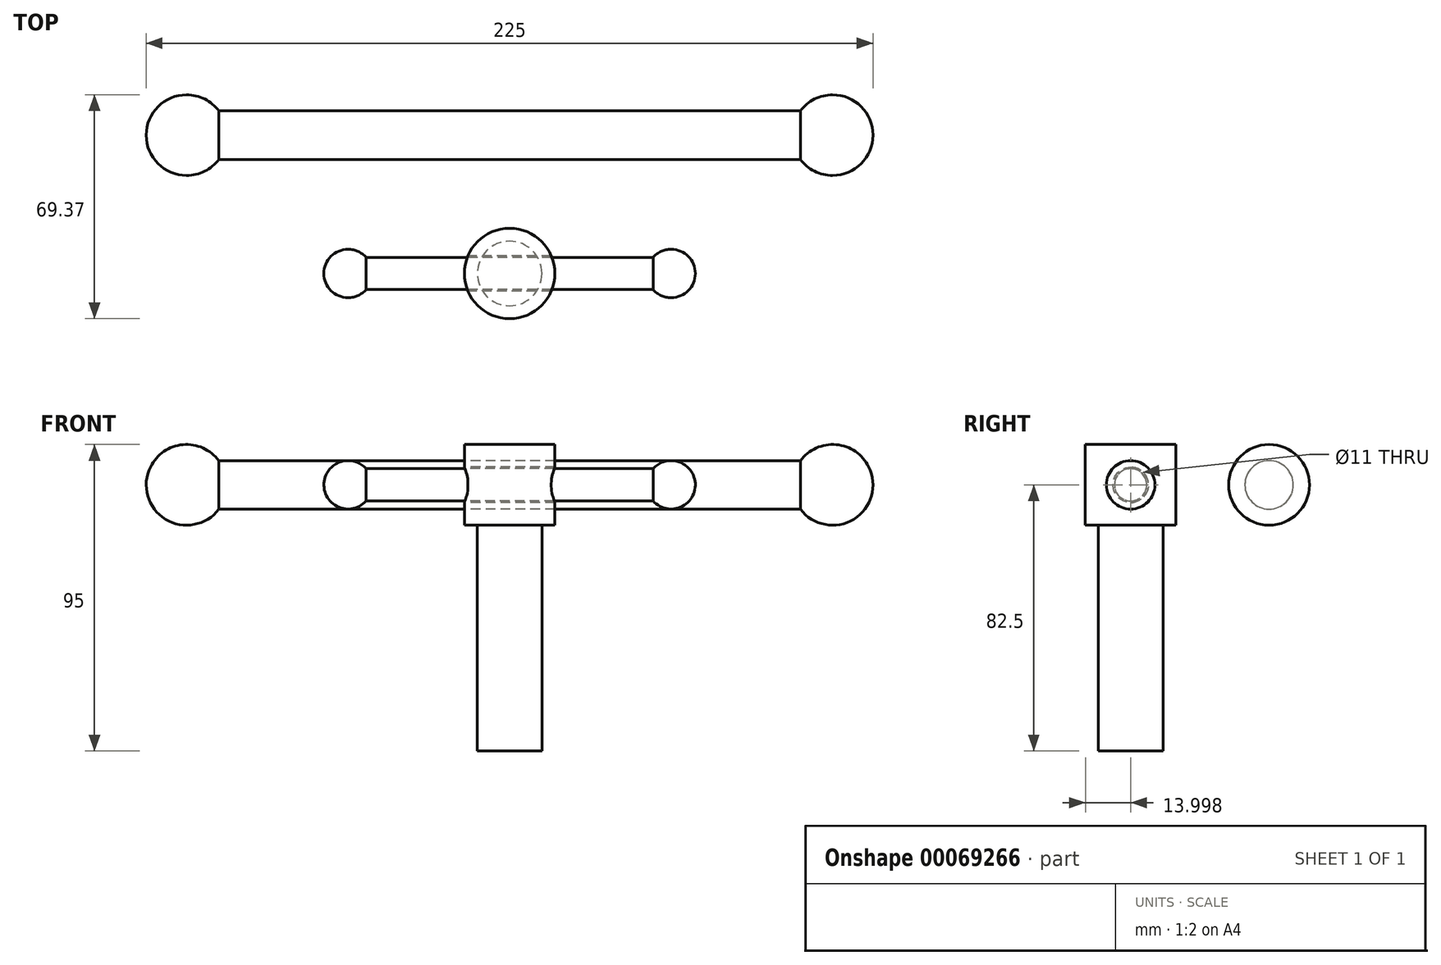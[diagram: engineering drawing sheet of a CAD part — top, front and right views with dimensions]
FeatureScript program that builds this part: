
annotation { "Feature Type Name" : "Feature", "Feature Type Description" : "" }
export const myFeature = defineFeature(function(context is Context, id is Id, definition is map)
    precondition{}
    {
        {
            var Q0;
            Q0=qCreatedBy(makeId("Right.planeOp"),FACE);
            var sketch = newSketch(context, id + "F0", { "sketchPlane" : qUnion([Q0])});
            skCircle(sketch, "E0", {"center": v(0, 0) * mm, "radius": 7.5 * mm});
            skSolve(sketch);
        }
        {
            var Q0;
            Q0=makeQuery(id+"F0.imprint","IMPRINT",FACE,{"disambiguationData":[TD([[makeQuery(id+"F0.imprint","IMPRINT",EDGE,{"derivedFrom":sQuery(id+"F0.wireOp",EDGE,"E0")}),1.0]])]});
            extrude(context, id + "F1", {"entities" : qUnion([Q0]), "endBound" : BoundingType.SYMMETRIC, "depth" : 200 * mm});
        }
        {
            var Q0;
            Q0=makeQuery(id+"F1.opExtrude","CAP_FACE",FACE,{"disambiguationData":[OSD([sQuery(id+"F0.wireOp",EDGE,"E0")])],"isStart":true});
            var sketch = newSketch(context, id + "F2", { "sketchPlane" : qUnion([Q0])});
            skArc(sketch, "E1", {"start": v(12.5, 0) * mm, "mid": v(0, 12.5) * mm, "end": v(-12.5, 0) * mm});
            skLineSegment(sketch, "E2", {"start": v(-12.5, 0) * mm, "end": v(12.5, 0) * mm});
            skSolve(sketch);
        }
        {
            var Q0;
            Q0 = qSketchRegion(id + "F2", true);
            var Q1;
            Q1=sQuery(id+"F2.wireOp",EDGE,"E2");
            revolve(context, id + "F3", {"operationType" : NewBodyOperationType.ADD, "entities" : qUnion([Q0]), "axis" : qUnion([Q1]), "revolveType" : RevolveType.FULL});
        }
        {
            var Q0;
            Q0=makeQuery(id+"F1.opExtrude","CAP_FACE",FACE,{"disambiguationData":[OSD([sQuery(id+"F0.wireOp",EDGE,"E0")])],"isStart":false});
            var sketch = newSketch(context, id + "F4", { "sketchPlane" : qUnion([Q0])});
            skArc(sketch, "E3.0", {"start": v(-12.5, 0) * mm, "mid": v(0, 12.5) * mm, "end": v(12.5, 0) * mm});
            skLineSegment(sketch, "E4.0", {"start": v(12.5, 0) * mm, "end": v(-12.5, 0) * mm});
            skSolve(sketch);
        }
        {
            var Q0;
            Q0 = qSketchRegion(id + "F4", true);
            var Q1;
            Q1=sQuery(id+"F4.wireOp",EDGE,"E4.0");
            revolve(context, id + "F5", {"operationType" : NewBodyOperationType.ADD, "entities" : qUnion([Q0]), "axis" : qUnion([Q1]), "revolveType" : RevolveType.FULL});
        }
        {
            var Q0;
            Q0=qCreatedBy(makeId("Top.planeOp"),FACE);
            var sketch = newSketch(context, id + "F6", { "sketchPlane" : qUnion([Q0])});
            skCircle(sketch, "E5", {"center": v(0, -42.87) * mm, "radius": 14 * mm});
            skSolve(sketch);
        }
        {
            var Q0;
            Q0 = qSketchRegion(id + "F6", true);
            extrude(context, id + "F7", {"entities" : qUnion([Q0]), "endBound" : BoundingType.SYMMETRIC, "depth" : 25 * mm});
        }
        {
            var Q0;
            Q0=qCreatedBy(makeId("Right.planeOp"),FACE);
            var sketch = newSketch(context, id + "F8", { "sketchPlane" : qUnion([Q0])});
            skCircle(sketch, "E6", {"center": v(-42.87, 0) * mm, "radius": 5.5 * mm});
            skLineSegment(sketch, "E7", {"start": v(-42.87, 0) * mm, "end": v(-42.87, 12.5) * mm, "construction": true});
            skSolve(sketch);
        }
        {
            var Q0;
            Q0 = qSketchRegion(id + "F8", true);
            extrude(context, id + "F9", {"entities" : qUnion([Q0]), "operationType" : NewBodyOperationType.REMOVE, "endBound" : BoundingType.THROUGH_ALL, "depth" : 25 * mm, "hasSecondDirection" : true, "secondDirectionBound" : SecondDirectionBoundingType.THROUGH_ALL, "secondDirectionOppositeDirection" : true, "secondDirectionDepth" : 25 * mm});
        }
        {
            var Q0;
            Q0=qCreatedBy(makeId("Right.planeOp"),FACE);
            var sketch = newSketch(context, id + "F10", { "sketchPlane" : qUnion([Q0])});
            skCircle(sketch, "E8", {"center": v(-42.87, 0) * mm, "radius": 5 * mm});
            skSolve(sketch);
        }
        {
            var Q0;
            Q0 = qSketchRegion(id + "F10", true);
            extrude(context, id + "F11", {"entities" : qUnion([Q0]), "endBound" : BoundingType.SYMMETRIC, "depth" : 100 * mm});
        }
        {
            var Q0;
            Q0=makeQuery(id+"F11.opExtrude","CAP_FACE",FACE,{"disambiguationData":[OSD([sQuery(id+"F10.wireOp",EDGE,"E8")])],"isStart":false});
            var sketch = newSketch(context, id + "F12", { "sketchPlane" : qUnion([Q0])});
            skArc(sketch, "E9", {"start": v(-35.37, 0) * mm, "mid": v(-42.87, 7.5) * mm, "end": v(-50.37, 0) * mm});
            skLineSegment(sketch, "E10", {"start": v(-50.37, 0) * mm, "end": v(-35.37, 0) * mm});
            skSolve(sketch);
        }
        {
            var Q0;
            Q0 = qSketchRegion(id + "F12", true);
            var Q1;
            Q1=sQuery(id+"F12.wireOp",EDGE,"E10");
            revolve(context, id + "F13", {"operationType" : NewBodyOperationType.ADD, "entities" : qUnion([Q0]), "axis" : qUnion([Q1]), "revolveType" : RevolveType.FULL});
        }
        {
            var Q0;
            Q0=makeQuery(id+"F11.opExtrude","CAP_FACE",FACE,{"disambiguationData":[OSD([sQuery(id+"F10.wireOp",EDGE,"E8")])],"isStart":true});
            var sketch = newSketch(context, id + "F14", { "sketchPlane" : qUnion([Q0])});
            skArc(sketch, "E11.0", {"start": v(35.37, 0) * mm, "mid": v(42.87, 7.5) * mm, "end": v(50.37, 0) * mm});
            skLineSegment(sketch, "E11.1", {"start": v(50.37, 0) * mm, "end": v(35.37, 0) * mm});
            skSolve(sketch);
        }
        {
            var Q0;
            Q0 = qSketchRegion(id + "F14", true);
            var Q1;
            Q1=sQuery(id+"F14.wireOp",EDGE,"E11.1");
            revolve(context, id + "F15", {"operationType" : NewBodyOperationType.ADD, "entities" : qUnion([Q0]), "axis" : qUnion([Q1]), "revolveType" : RevolveType.FULL});
        }
        {
            var Q0;
            Q0=makeQuery(id+"F7.opExtrude","CAP_FACE",FACE,{"disambiguationData":[OSD([sQuery(id+"F6.wireOp",EDGE,"E5")])],"isStart":true});
            var sketch = newSketch(context, id + "F16", { "sketchPlane" : qUnion([Q0])});
            skCircle(sketch, "E12", {"center": v(0, 42.87) * mm, "radius": 10 * mm});
            skSolve(sketch);
        }
        {
            var Q0;
            Q0 = qSketchRegion(id + "F16", true);
            extrude(context, id + "F17", {"entities" : qUnion([Q0]), "operationType" : NewBodyOperationType.ADD, "depth" : 70 * mm});
        }
    });
